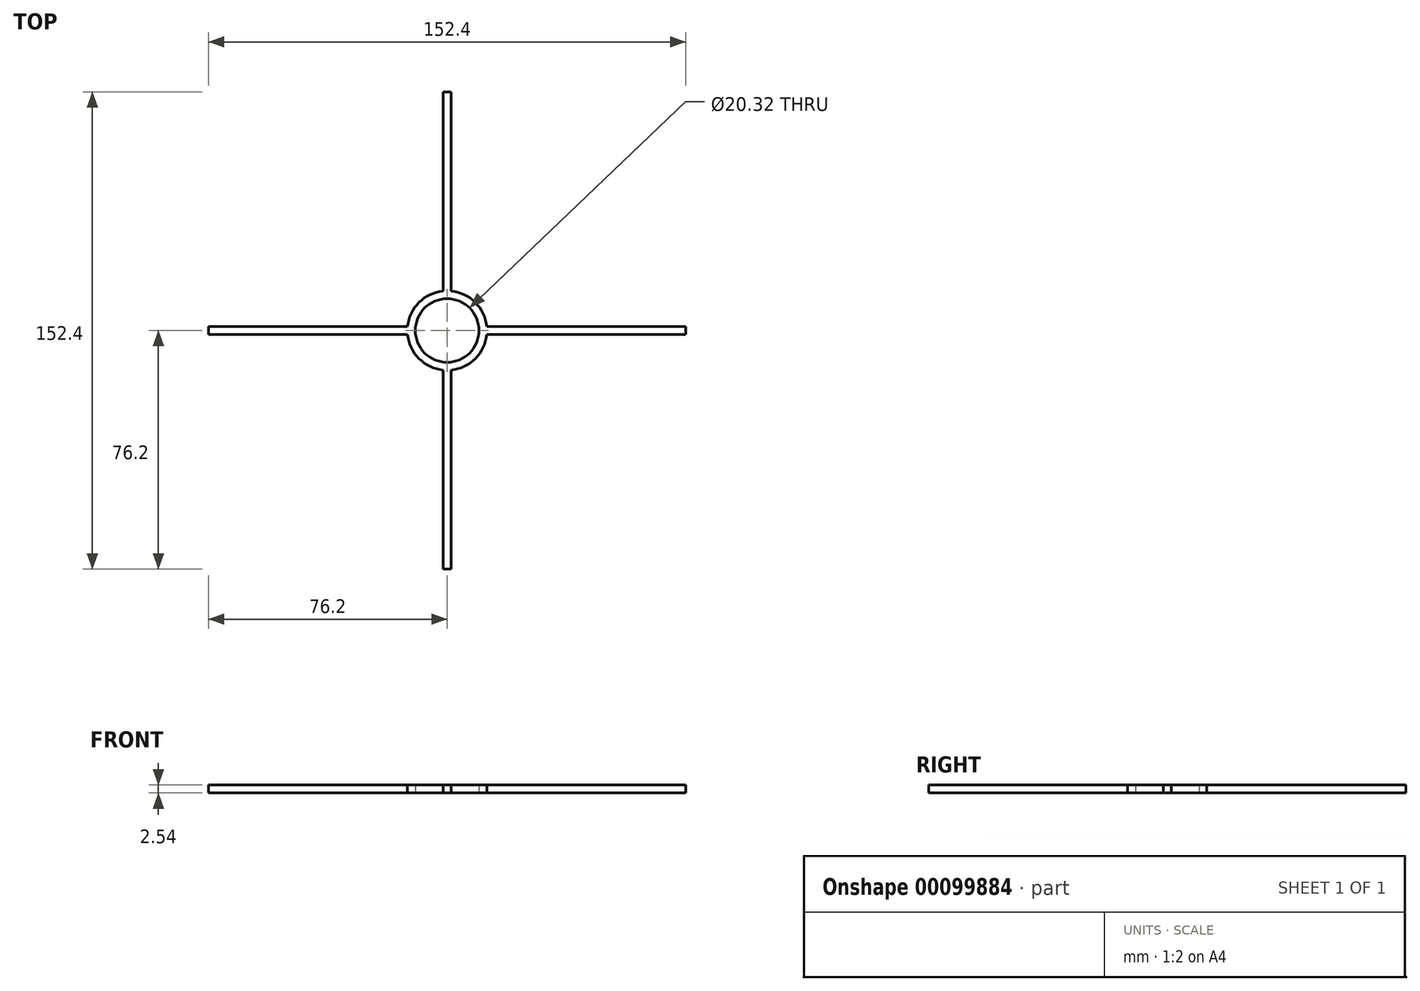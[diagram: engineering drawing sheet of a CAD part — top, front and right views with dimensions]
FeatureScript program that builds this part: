
annotation { "Feature Type Name" : "Feature", "Feature Type Description" : "" }
export const myFeature = defineFeature(function(context is Context, id is Id, definition is map)
    precondition{}
    {
        {
            var Q0;
            Q0=qCreatedBy(makeId("Top.planeOp"),FACE);
            var sketch = newSketch(context, id + "F0", { "sketchPlane" : qUnion([Q0])});
            skLineSegment(sketch, "E0.bottom", {"start": v(76.2, 1.27) * mm, "end": v(-76.2, 1.27) * mm});
            skLineSegment(sketch, "E0.top", {"start": v(76.2, -1.27) * mm, "end": v(-76.2, -1.27) * mm});
            skLineSegment(sketch, "E0.left", {"start": v(76.2, 1.27) * mm, "end": v(76.2, -1.27) * mm});
            skLineSegment(sketch, "E0.right", {"start": v(-76.2, 1.27) * mm, "end": v(-76.2, -1.27) * mm});
            skPoint(sketch, "E0.middle", {"position": v(0, 0) * mm});
            skSolve(sketch);
        }
        {
            var Q0;
            Q0 = qSketchRegion(id + "F0", true);
            extrude(context, id + "F1", {"entities" : qUnion([Q0]), "depth" : 2.54 * mm});
        }
        {
            var Q0;
            Q0=qCreatedBy(makeId("Top.planeOp"),FACE);
            var sketch = newSketch(context, id + "F2", { "sketchPlane" : qUnion([Q0])});
            skCircle(sketch, "E1", {"center": v(0, 0) * mm, "radius": 12.7 * mm});
            skLineSegment(sketch, "E2.bottom", {"start": v(-1.27, -76.2) * mm, "end": v(1.27, -76.2) * mm});
            skLineSegment(sketch, "E2.top", {"start": v(-1.27, 76.2) * mm, "end": v(1.27, 76.2) * mm});
            skLineSegment(sketch, "E2.left", {"start": v(-1.27, -76.2) * mm, "end": v(-1.27, 76.2) * mm});
            skLineSegment(sketch, "E2.right", {"start": v(1.27, -76.2) * mm, "end": v(1.27, 76.2) * mm});
            skSolve(sketch);
        }
        {
            var Q0;
            Q0=makeQuery(id+"F2.imprint","IMPRINT",FACE,{"disambiguationData":[TD([[makeQuery(id+"F2.imprint","IMPRINT",EDGE,{"derivedFrom":sQuery(id+"F2.wireOp",EDGE,"E1")}),1.0]])]});
            extrude(context, id + "F3", {"entities" : qUnion([Q0]), "operationType" : NewBodyOperationType.ADD, "depth" : 2.54 * mm});
        }
        {
            var Q0;
            Q0 = qSketchRegion(id + "F2", true);
            extrude(context, id + "F4", {"entities" : qUnion([Q0]), "operationType" : NewBodyOperationType.ADD, "depth" : 2.54 * mm});
        }
        {
            var Q0;
            {var subQ0=sQuery(id+"F2.wireOp",EDGE,"E2.right");var subQ1=sQuery(id+"F2.wireOp",EDGE,"E2.left");var subQ2=sQuery(id+"F2.wireOp",EDGE,"E1");Q0=makeQuery(id+"F4.boolean.opBoolean","MERGE",FACE,{"derivedFrom":[makeQuery(id+"F3.boolean.opBoolean","MERGE",FACE,{"derivedFrom":[makeQuery(id+"F1.opExtrude","CAP_FACE",FACE,{"disambiguationData":[OSD([sQuery(id+"F0.wireOp",EDGE,"E0.bottom"),sQuery(id+"F0.wireOp",EDGE,"E0.top"),sQuery(id+"F0.wireOp",EDGE,"E0.left"),sQuery(id+"F0.wireOp",EDGE,"E0.right")])],"isStart":true}),makeQuery(id+"F3.opExtrude","CAP_FACE",FACE,{"disambiguationData":[OSD([subQ2,subQ1,subQ0])],"isStart":true})]}),makeQuery(id+"F4.opExtrude","CAP_FACE",FACE,{"disambiguationData":[OSD([subQ2,sQuery(id+"F2.wireOp",EDGE,"E2.bottom"),sQuery(id+"F2.wireOp",EDGE,"E2.top"),subQ1,subQ0])],"isStart":true})]});}
            var Q1;
            {var subQ0=sQuery(id+"F2.wireOp",EDGE,"E2.right");var subQ1=sQuery(id+"F2.wireOp",EDGE,"E2.left");var subQ2=sQuery(id+"F2.wireOp",EDGE,"E1");Q1=makeQuery(id+"F4.boolean.opBoolean","MERGE",FACE,{"derivedFrom":[makeQuery(id+"F3.boolean.opBoolean","MERGE",FACE,{"derivedFrom":[makeQuery(id+"F1.opExtrude","CAP_FACE",FACE,{"disambiguationData":[OSD([sQuery(id+"F0.wireOp",EDGE,"E0.bottom"),sQuery(id+"F0.wireOp",EDGE,"E0.top"),sQuery(id+"F0.wireOp",EDGE,"E0.left"),sQuery(id+"F0.wireOp",EDGE,"E0.right")])],"isStart":false}),makeQuery(id+"F3.opExtrude","CAP_FACE",FACE,{"disambiguationData":[OSD([subQ2,subQ1,subQ0])],"isStart":false})]}),makeQuery(id+"F4.opExtrude","CAP_FACE",FACE,{"disambiguationData":[OSD([subQ2,sQuery(id+"F2.wireOp",EDGE,"E2.bottom"),sQuery(id+"F2.wireOp",EDGE,"E2.top"),subQ1,subQ0])],"isStart":false})]});}
            shell(context, id + "F5", {"entities" : qUnion([Q0, Q1]), "thickness" : 2.54 * mm});
        }
    });
